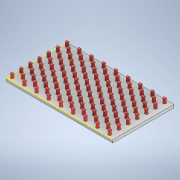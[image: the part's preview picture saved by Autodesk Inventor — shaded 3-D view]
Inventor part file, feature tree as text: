
AUTODESK INVENTOR PART (.ipt)
format: ipt  version: 2020 (Build 240168000, 168)  size: 499,200 bytes
history: native  units: mm
features: other x113, sketch x112
ambient origin geometry x8: Origin, YZ Plane, XZ Plane, XY Plane, X Axis, Y Axis, Z Axis, Center Point
bodies: Solid1 (feature_tree)
feature tree (225):
  other  "final_soft.iam"
  other  "base_soft.ipt:1"
  other  "soft_1.ipt:1"
  other  "soft_1.ipt:2"
  other  "soft_1.ipt:3"
  other  "soft_1.ipt:4"
  other  "soft_1.ipt:5"
  other  "soft_1.ipt:6"
  other  "soft_1.ipt:7"
  other  "soft_1.ipt:8"
  other  "soft_1.ipt:9"
  other  "soft_1.ipt:10"
  other  "soft_1.ipt:11"
  other  "soft_1.ipt:12"
  other  "soft_1.ipt:13"
  other  "soft_1.ipt:14"
  other  "soft_1.ipt:15"
  other  "soft_1.ipt:16"
  other  "soft_1.ipt:17"
  other  "soft_1.ipt:18"
  other  "soft_1.ipt:19"
  other  "soft_1.ipt:20"
  other  "soft_1.ipt:21"
  other  "soft_1.ipt:22"
  other  "soft_1.ipt:23"
  other  "soft_1.ipt:24"
  other  "soft_1.ipt:25"
  other  "soft_1.ipt:26"
  other  "soft_1.ipt:27"
  other  "soft_1.ipt:28"
  other  "soft_1.ipt:29"
  other  "soft_1.ipt:30"
  other  "soft_1.ipt:31"
  other  "soft_1.ipt:32"
  other  "soft_1.ipt:33"
  other  "soft_1.ipt:34"
  other  "soft_1.ipt:35"
  other  "soft_1.ipt:36"
  other  "soft_1.ipt:37"
  other  "soft_1.ipt:38"
  other  "soft_1.ipt:39"
  other  "soft_1.ipt:40"
  other  "soft_1.ipt:41"
  other  "soft_1.ipt:42"
  other  "soft_1.ipt:43"
  other  "soft_1.ipt:44"
  other  "soft_1.ipt:45"
  other  "soft_1.ipt:46"
  other  "soft_1.ipt:47"
  other  "soft_1.ipt:48"
  other  "soft_1.ipt:49"
  other  "soft_1.ipt:50"
  other  "soft_1.ipt:51"
  other  "soft_1.ipt:52"
  other  "soft_1.ipt:53"
  other  "soft_1.ipt:54"
  other  "soft_1.ipt:55"
  other  "soft_1.ipt:56"
  other  "soft_1.ipt:57"
  other  "soft_1.ipt:58"
  other  "soft_1.ipt:59"
  other  "soft_1.ipt:60"
  other  "soft_1.ipt:61"
  other  "soft_1.ipt:62"
  other  "soft_1.ipt:63"
  other  "soft_1.ipt:64"
  other  "soft_1.ipt:65"
  other  "soft_1.ipt:66"
  other  "soft_1.ipt:67"
  other  "soft_1.ipt:68"
  other  "soft_1.ipt:69"
  other  "soft_1.ipt:70"
  other  "soft_1.ipt:71"
  other  "soft_1.ipt:72"
  other  "soft_1.ipt:73"
  other  "soft_1.ipt:74"
  other  "soft_1.ipt:75"
  other  "soft_1.ipt:76"
  other  "soft_1.ipt:77"
  other  "soft_1.ipt:78"
  other  "soft_1.ipt:79"
  other  "soft_1.ipt:80"
  other  "soft_1.ipt:81"
  other  "soft_1.ipt:82"
  other  "soft_1.ipt:83"
  other  "soft_1.ipt:84"
  other  "soft_1.ipt:85"
  other  "soft_1.ipt:86"
  other  "soft_1.ipt:87"
  other  "soft_1.ipt:88"
  other  "soft_1.ipt:89"
  other  "soft_1.ipt:90"
  other  "soft_1.ipt:91"
  other  "soft_1.ipt:92"
  other  "soft_1.ipt:93"
  other  "soft_1.ipt:94"
  other  "soft_1.ipt:95"
  other  "soft_1.ipt:96"
  other  "soft_1.ipt:97"
  other  "soft_1.ipt:98"
  other  "soft_1.ipt:99"
  other  "soft_1.ipt:100"
  other  "soft_1.ipt:101"
  other  "soft_1.ipt:102"
  other  "soft_1.ipt:103"
  other  "soft_1.ipt:104"
  other  "soft_1.ipt:105"
  other  "soft_1.ipt:106"
  other  "soft_1.ipt:107"
  other  "soft_1.ipt:108"
  other  "soft_1.ipt:109"
  other  "soft_1.ipt:110"
  other  "soft_1.ipt:111"
  sketch  "Sketch2"
  sketch  "Sketch4"
  sketch  "Sketch4_1"  dims[d0=10.0mm]
  sketch  "Sketch4_2"
  sketch  "Sketch4_3"
  sketch  "Sketch4_4"
  sketch  "Sketch4_5"
  sketch  "Sketch4_6"
  sketch  "Sketch4_7"
  sketch  "Sketch4_8"
  sketch  "Sketch4_9"
  sketch  "Sketch4_10"
  sketch  "Sketch4_11"
  sketch  "Sketch4_12"
  sketch  "Sketch4_13"
  sketch  "Sketch4_14"
  sketch  "Sketch4_15"
  sketch  "Sketch4_16"
  sketch  "Sketch4_17"
  sketch  "Sketch4_18"
  sketch  "Sketch4_19"
  sketch  "Sketch4_20"
  sketch  "Sketch4_21"
  sketch  "Sketch4_22"
  sketch  "Sketch4_23"
  sketch  "Sketch4_24"
  sketch  "Sketch4_25"
  sketch  "Sketch4_26"
  sketch  "Sketch4_27"
  sketch  "Sketch4_28"
  sketch  "Sketch4_29"
  sketch  "Sketch4_30"
  sketch  "Sketch4_31"
  sketch  "Sketch4_32"
  sketch  "Sketch4_33"
  sketch  "Sketch4_34"
  sketch  "Sketch4_35"
  sketch  "Sketch4_36"
  sketch  "Sketch4_37"
  sketch  "Sketch4_38"
  sketch  "Sketch4_39"
  sketch  "Sketch4_40"
  sketch  "Sketch4_41"
  sketch  "Sketch4_42"
  sketch  "Sketch4_43"
  sketch  "Sketch4_44"
  sketch  "Sketch4_45"
  sketch  "Sketch4_46"
  sketch  "Sketch4_47"
  sketch  "Sketch4_48"
  sketch  "Sketch4_49"
  sketch  "Sketch4_50"
  sketch  "Sketch4_51"
  sketch  "Sketch4_52"
  sketch  "Sketch4_53"
  sketch  "Sketch4_54"
  sketch  "Sketch4_55"
  sketch  "Sketch4_56"
  sketch  "Sketch4_57"
  sketch  "Sketch4_58"
  sketch  "Sketch4_59"
  sketch  "Sketch4_60"
  sketch  "Sketch4_61"
  sketch  "Sketch4_62"
  sketch  "Sketch4_63"
  sketch  "Sketch4_64"
  sketch  "Sketch4_65"
  sketch  "Sketch4_66"
  sketch  "Sketch4_67"
  sketch  "Sketch4_68"
  sketch  "Sketch4_69"
  sketch  "Sketch4_70"
  sketch  "Sketch4_71"
  sketch  "Sketch4_72"
  sketch  "Sketch4_73"
  sketch  "Sketch4_74"
  sketch  "Sketch4_75"
  sketch  "Sketch4_76"
  sketch  "Sketch4_77"
  sketch  "Sketch4_78"
  sketch  "Sketch4_79"
  sketch  "Sketch4_80"
  sketch  "Sketch4_81"
  sketch  "Sketch4_82"
  sketch  "Sketch4_83"
  sketch  "Sketch4_84"
  sketch  "Sketch4_85"
  sketch  "Sketch4_86"
  sketch  "Sketch4_87"
  sketch  "Sketch4_88"
  sketch  "Sketch4_89"
  sketch  "Sketch4_90"
  sketch  "Sketch4_91"
  sketch  "Sketch4_92"
  sketch  "Sketch4_93"
  sketch  "Sketch4_94"
  sketch  "Sketch4_95"
  sketch  "Sketch4_96"
  sketch  "Sketch4_97"
  sketch  "Sketch4_98"
  sketch  "Sketch4_99"
  sketch  "Sketch4_100"
  sketch  "Sketch4_101"
  sketch  "Sketch4_102"
  sketch  "Sketch4_103"
  sketch  "Sketch4_104"
  sketch  "Sketch4_105"
  sketch  "Sketch4_106"
  sketch  "Sketch4_107"
  sketch  "Sketch4_108"
  sketch  "Sketch4_109"
  sketch  "Sketch4_110"
